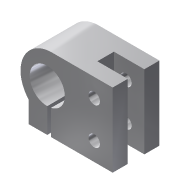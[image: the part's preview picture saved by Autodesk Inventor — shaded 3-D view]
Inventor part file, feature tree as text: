
AUTODESK INVENTOR PART (.ipt)
format: ipt  version: 2015 (Build 190159000, 159)  size: 167,424 bytes
history: native  units: mm
features: sketch x4, extrude x3, revolve x1
ambient origin geometry x8: Origin, YZ Plane, XZ Plane, XY Plane, X Axis, Y Axis, Z Axis, Center Point
bodies: Solid1 (feature_tree)
feature tree (8):
  extrude  "Extrusion1"  Depth=40.0mm
  extrude  "Extrusion2"  Depth=10.0mm
  revolve  "Revolution2"  [1 undecoded]
  extrude  "Extrusion3"  Depth=45.5mm
  sketch  "Sketch1"  dims[d0=50.0mm d1=40.0mm]
  sketch  "Sketch2"  dims[d2=10.0mm d3=10.0mm]
  sketch  "Sketch6"  dims[d4=20.0mm d5=6.2mm]
  sketch  "Sketch7"  dims[d6=6.2mm d7=45.5mm d8=35.5mm d9=4.5mm d10=4.5mm d13=12.5mm d14=12.5mm d15=2.0mm d16=25.4mm d17=0.0mm d18=8.2mm d19=16.5mm d20=9.0mm d21=25.4mm d22=0.0mm d23=10.0mm d35=14.835299mm d36=10.0mm d37=14.835299mm d43=30.0mm d44=90.0deg d45=30.0mm d47=30.0mm d48=16.580628mm d49=9.5mm d50=90.0deg d51=10.0mm d52=0.0mm]
note: 1 required parameter value undecoded (feature->parameter linkage not recoverable at this tier; creation-order binding heuristic only, values carry confidence <= 0.55)
